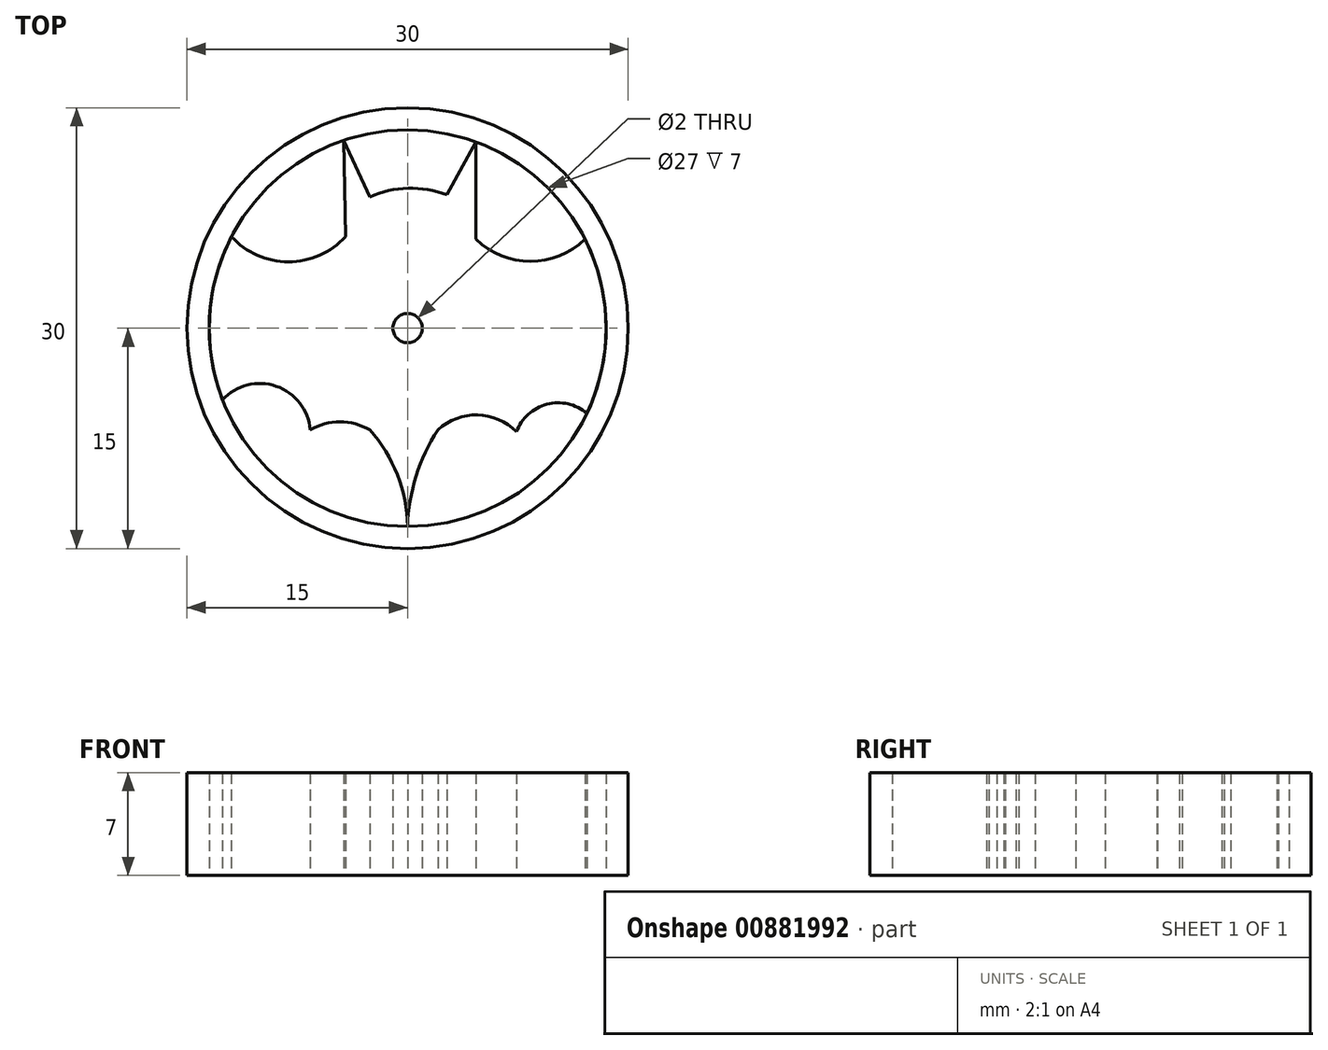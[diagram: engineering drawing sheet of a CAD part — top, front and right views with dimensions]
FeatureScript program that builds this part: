
annotation { "Feature Type Name" : "Feature", "Feature Type Description" : "" }
export const myFeature = defineFeature(function(context is Context, id is Id, definition is map)
    precondition{}
    {
        {
            var Q0;
            Q0=qCreatedBy(makeId("Top.planeOp"),FACE);
            var sketch = newSketch(context, id + "F0", { "sketchPlane" : qUnion([Q0])});
            skCircle(sketch, "E0", {"center": v(0, 0) * mm, "radius": 15 * mm});
            skCircle(sketch, "E1", {"center": v(0, 0) * mm, "radius": 13.5 * mm});
            skLineSegment(sketch, "E2", {"start": v(4.64, 12.68) * mm, "end": v(2.67, 9.08) * mm});
            skLineSegment(sketch, "E3", {"start": v(-4.36, 12.78) * mm, "end": v(-2.58, 8.94) * mm});
            skArc(sketch, "E4", {"start": v(2.67, 9.08) * mm, "mid": v(0.03, 9.53) * mm, "end": v(-2.58, 8.94) * mm});
            skLineSegment(sketch, "E5", {"start": v(4.64, 12.68) * mm, "end": v(4.64, 6.05) * mm});
            skLineSegment(sketch, "E6", {"start": v(-4.22, 6.23) * mm, "end": v(-4.36, 12.78) * mm});
            skArc(sketch, "E7", {"start": v(4.64, 6.05) * mm, "mid": v(8.36, 4.54) * mm, "end": v(12.07, 6.05) * mm});
            skArc(sketch, "E8", {"start": v(-11.98, 6.23) * mm, "mid": v(-8.1, 4.51) * mm, "end": v(-4.22, 6.23) * mm});
            skArc(sketch, "E9", {"start": v(12.2, -5.79) * mm, "mid": v(9.47, -5.18) * mm, "end": v(7.4, -7.06) * mm});
            skArc(sketch, "E10", {"start": v(-6.62, -6.92) * mm, "mid": v(-8.94, -3.95) * mm, "end": v(-12.6, -4.87) * mm});
            skArc(sketch, "E11", {"start": v(7.4, -7.06) * mm, "mid": v(4.76, -5.9) * mm, "end": v(2.06, -6.92) * mm});
            skArc(sketch, "E12", {"start": v(-2.58, -6.92) * mm, "mid": v(-4.6, -6.37) * mm, "end": v(-6.62, -6.92) * mm});
            skPoint(sketch, "E13.start.orphan", {"position": v(0, -9.58) * mm});
            skArc(sketch, "E14", {"start": v(2.06, -6.92) * mm, "mid": v(0.57, -10.07) * mm, "end": v(0, -13.5) * mm});
            skArc(sketch, "E15", {"start": v(0, -13.5) * mm, "mid": v(-0.7, -9.98) * mm, "end": v(-2.58, -6.92) * mm});
            skSolve(sketch);
        }
        {
            var Q0;
            Q0 = qSketchRegion(id + "F0", true);
            extrude(context, id + "F1", {"entities" : qUnion([Q0]), "depth" : 7 * mm, "offsetDistance" : 25 * mm});
        }
        {
            var Q0;
            Q0=makeQuery(id+"F0.imprint","IMPRINT",FACE,{"disambiguationData":[TD([[makeQuery(id+"F0.imprint","IMPRINT",EDGE,{"derivedFrom":sQuery(id+"F0.wireOp",EDGE,"E2")}),1.0]])]});
            extrude(context, id + "F2", {"entities" : qUnion([Q0]), "depth" : 7 * mm, "offsetDistance" : 25 * mm});
        }
        {
            var Q0;
            Q0=qCreatedBy(makeId("Top.planeOp"),FACE);
            var sketch = newSketch(context, id + "F3", { "sketchPlane" : qUnion([Q0])});
            skCircle(sketch, "E16", {"center": v(0, 0) * mm, "radius": 1 * mm});
            skSolve(sketch);
        }
        {
            var Q0;
            Q0 = qSketchRegion(id + "F3", true);
            extrude(context, id + "F4", {"entities" : qUnion([Q0]), "operationType" : NewBodyOperationType.REMOVE, "endBound" : BoundingType.THROUGH_ALL, "depth" : 25 * mm, "offsetDistance" : 25 * mm});
        }
    });
